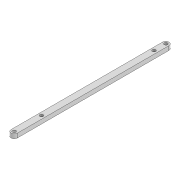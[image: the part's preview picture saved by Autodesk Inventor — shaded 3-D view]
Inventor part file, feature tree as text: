
AUTODESK INVENTOR PART (.ipt)
format: ipt  version: 2022 (Build 260153000, 153)  size: 91,648 bytes
history: native  units: mm
features: extrude x1, sketch x1
ambient origin geometry x8: Origin, YZ Plane, XZ Plane, XY Plane, X Axis, Y Axis, Z Axis, Center Point
bodies: Solid1 (feature_tree)
feature tree (2):
  extrude  "Extrusion1"  Depth=133.688mm
  sketch  "Sketch1"  dims[d0=3.2mm d1=3.2mm d2=6.0mm d3=144.957mm d6=4.0mm d7=0.0mm d10=3.2mm d11=26.085mm d12=3.2mm d13=133.688mm]
